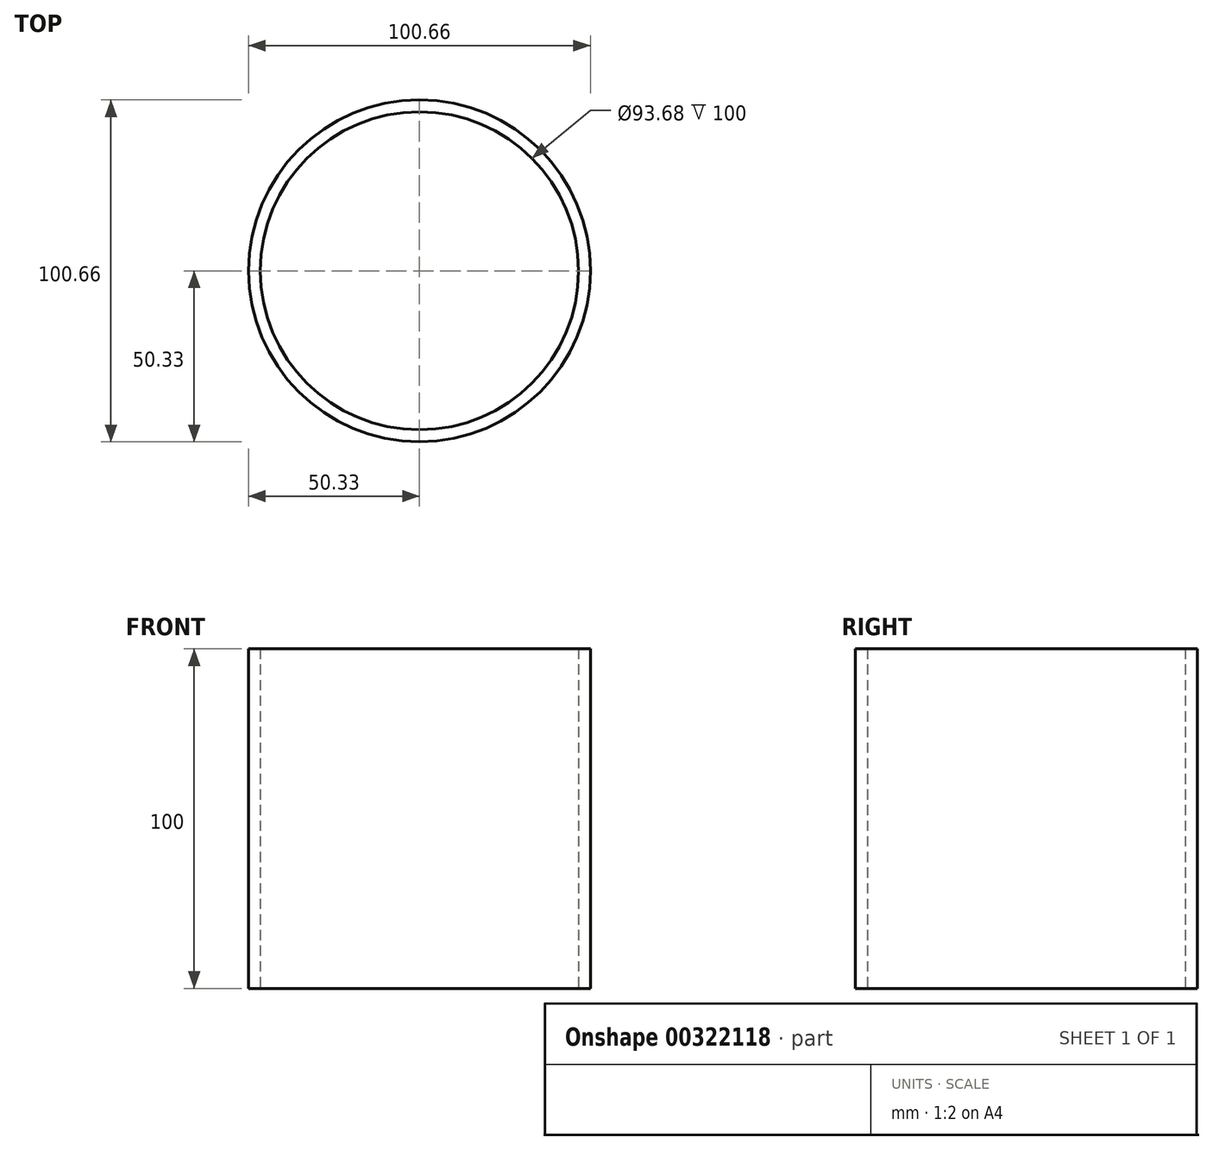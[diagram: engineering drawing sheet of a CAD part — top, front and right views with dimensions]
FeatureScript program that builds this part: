
annotation { "Feature Type Name" : "Feature", "Feature Type Description" : "" }
export const myFeature = defineFeature(function(context is Context, id is Id, definition is map)
    precondition{}
    {
        {
            var Q0;
            Q0=qCreatedBy(makeId("Top.planeOp"),FACE);
            var sketch = newSketch(context, id + "F0", { "sketchPlane" : qUnion([Q0])});
            skCircle(sketch, "E0", {"center": v(0, 0) * mm, "radius": 50.33 * mm});
            skCircle(sketch, "E1", {"center": v(0, 0) * mm, "radius": 46.84 * mm});
            skSolve(sketch);
        }
        {
            var Q0;
            Q0=makeQuery(id+"F0.imprint","IMPRINT",FACE,{"disambiguationData":[TD([[makeQuery(id+"F0.imprint","IMPRINT",EDGE,{"derivedFrom":sQuery(id+"F0.wireOp",EDGE,"E0")}),1.0]])]});
            extrude(context, id + "F1", {"entities" : qUnion([Q0]), "depth" : 100 * mm});
        }
    });
